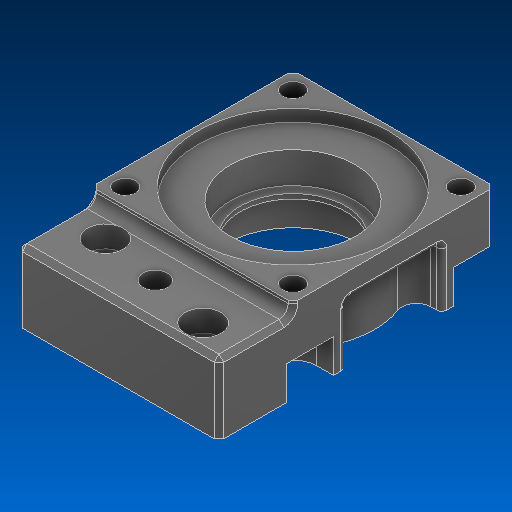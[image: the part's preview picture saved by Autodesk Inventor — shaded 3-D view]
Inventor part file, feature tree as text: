
AUTODESK INVENTOR PART (.ipt)
format: ipt  version: 2022.2 (Build 262287000, 287)  size: 274,944 bytes
history: native  units: in
note: dims shown in document units (in); Inventor stores cm internally (conversion verified against a paired STEP export)
features: fillet x1
ambient origin geometry x8: Origin, YZ Plane, XZ Plane, XY Plane, X Axis, Y Axis, Z Axis, Center Point
bodies: Solid1 (feature_tree)
feature tree (1):
  fillet  "Fillet5"  [1 undecoded]
note: 1 required parameter value undecoded (feature->parameter linkage not recoverable at this tier; creation-order binding heuristic only, values carry confidence <= 0.55)
